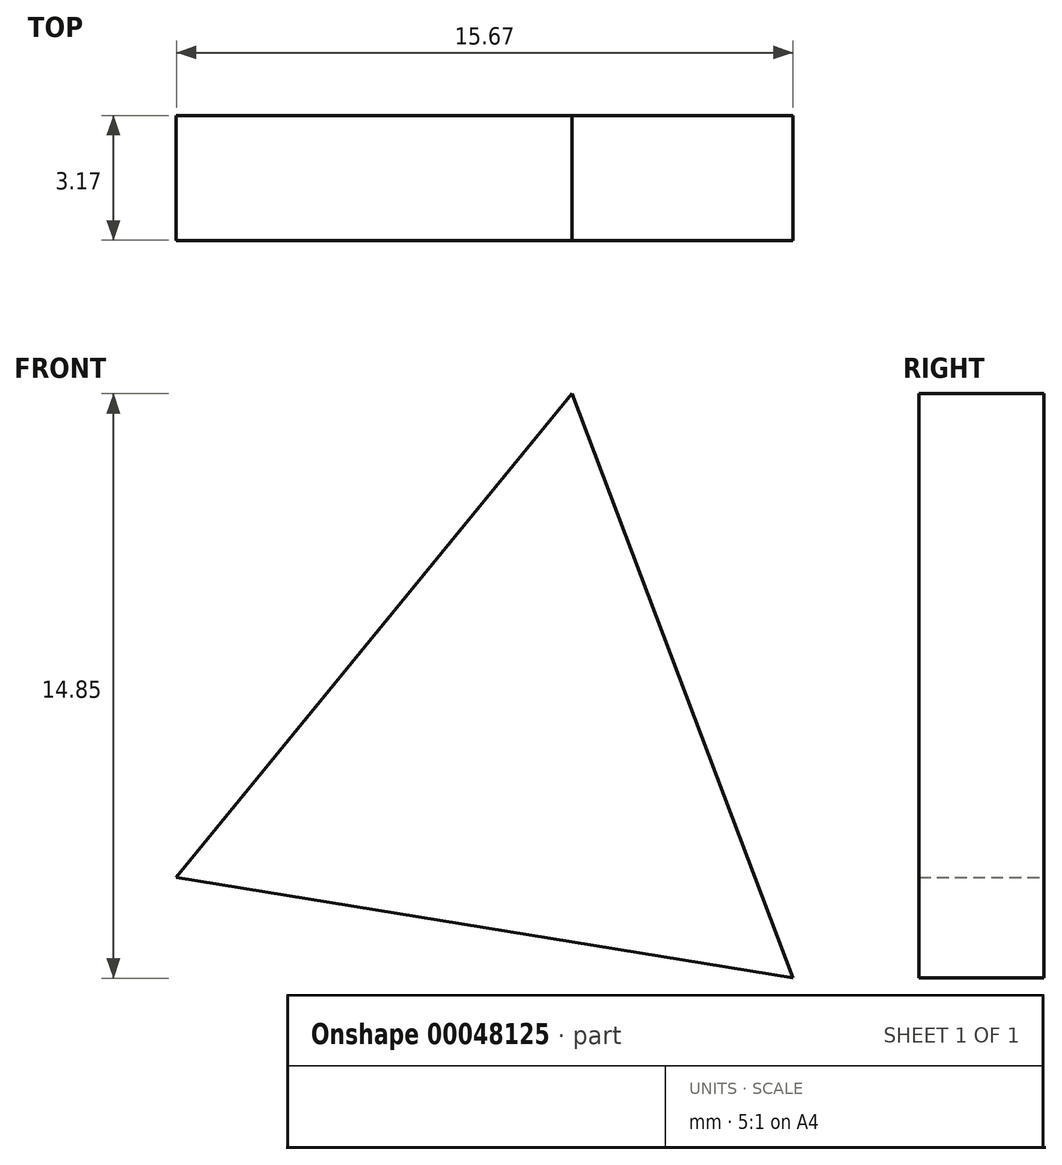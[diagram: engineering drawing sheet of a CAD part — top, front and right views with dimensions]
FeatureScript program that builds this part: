
annotation { "Feature Type Name" : "Feature", "Feature Type Description" : "" }
export const myFeature = defineFeature(function(context is Context, id is Id, definition is map)
    precondition{}
    {
        {
            var Q0;
            Q0=qCreatedBy(makeId("Front.planeOp"),FACE);
            var sketch = newSketch(context, id + "F0", { "sketchPlane" : qUnion([Q0])});
            skLineSegment(sketch, "E0", {"start": v(0, 0) * mm, "end": v(5.62, -14.85) * mm});
            skLineSegment(sketch, "E1", {"start": v(5.62, -14.85) * mm, "end": v(-10.05, -12.29) * mm});
            skLineSegment(sketch, "E2", {"start": v(-10.05, -12.29) * mm, "end": v(0, 0) * mm});
            skSolve(sketch);
        }
        {
            var Q0;
            Q0=makeQuery(id+"F0.imprint","IMPRINT",FACE,{"disambiguationData":[TD([[makeQuery(id+"F0.imprint","IMPRINT",EDGE,{"derivedFrom":sQuery(id+"F0.wireOp",EDGE,"E0")}),-1.0]])]});
            extrude(context, id + "F1", {"entities" : qUnion([Q0]), "depth" : 3.17 * mm});
        }
    });
